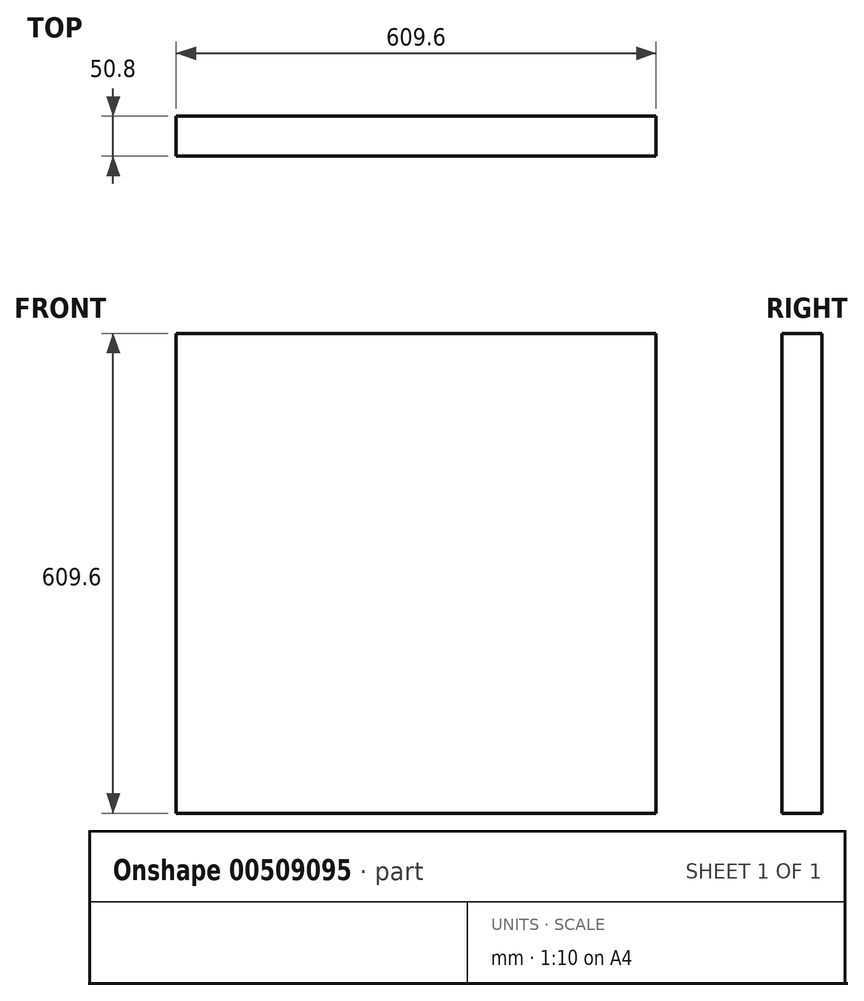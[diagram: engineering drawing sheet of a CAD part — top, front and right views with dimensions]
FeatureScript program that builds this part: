
annotation { "Feature Type Name" : "Feature", "Feature Type Description" : "" }
export const myFeature = defineFeature(function(context is Context, id is Id, definition is map)
    precondition{}
    {
        {
            var Q0;
            Q0=qCreatedBy(makeId("Front.planeOp"),FACE);
            var sketch = newSketch(context, id + "F0", { "sketchPlane" : qUnion([Q0])});
            skLineSegment(sketch, "E0.bottom", {"start": v(304.8, 304.8) * mm, "end": v(-304.8, 304.8) * mm});
            skLineSegment(sketch, "E0.top", {"start": v(304.8, -304.8) * mm, "end": v(-304.8, -304.8) * mm});
            skLineSegment(sketch, "E0.left", {"start": v(304.8, 304.8) * mm, "end": v(304.8, -304.8) * mm});
            skLineSegment(sketch, "E0.right", {"start": v(-304.8, 304.8) * mm, "end": v(-304.8, -304.8) * mm});
            skPoint(sketch, "E0.middle", {"position": v(0, 0) * mm});
            skSolve(sketch);
        }
        {
            var Q0;
            Q0=makeQuery(id+"F0.imprint","IMPRINT",FACE,{"disambiguationData":[TD([[makeQuery(id+"F0.imprint","IMPRINT",EDGE,{"derivedFrom":sQuery(id+"F0.wireOp",EDGE,"E0.bottom")}),1.0]])]});
            extrude(context, id + "F1", {"entities" : qUnion([Q0]), "depth" : 50.8 * mm});
        }
    });
